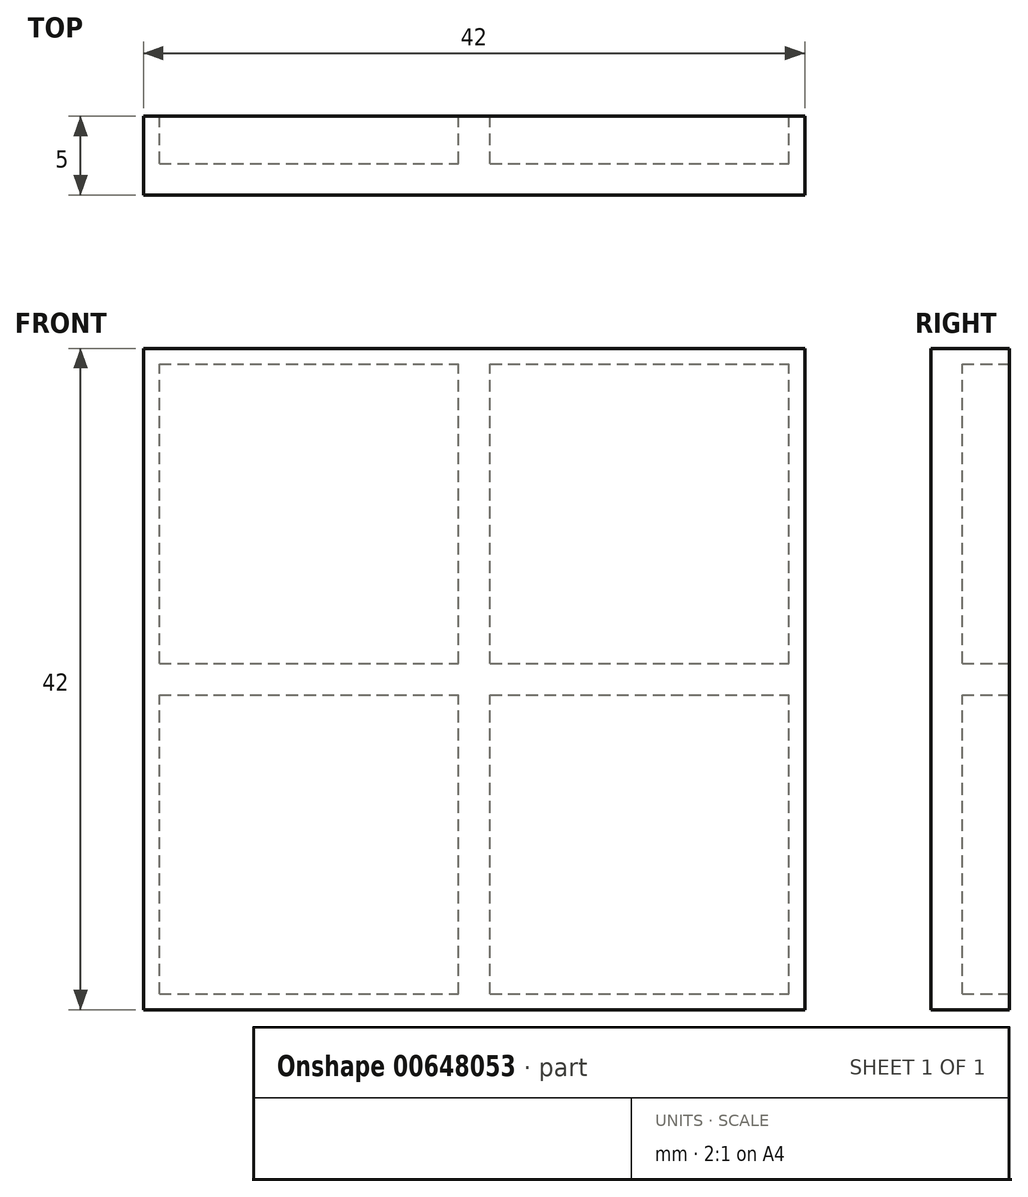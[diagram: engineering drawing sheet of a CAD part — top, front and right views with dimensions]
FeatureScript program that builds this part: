
annotation { "Feature Type Name" : "Feature", "Feature Type Description" : "" }
export const myFeature = defineFeature(function(context is Context, id is Id, definition is map)
    precondition{}
    {
        {
            var Q0;
            Q0=qCreatedBy(makeId("Front.planeOp"),FACE);
            var sketch = newSketch(context, id + "F0", { "sketchPlane" : qUnion([Q0])});
            skLineSegment(sketch, "E0.bottom", {"start": v(-21, 21) * mm, "end": v(21, 21) * mm});
            skLineSegment(sketch, "E0.top", {"start": v(-21, -21) * mm, "end": v(21, -21) * mm});
            skLineSegment(sketch, "E0.left", {"start": v(-21, 21) * mm, "end": v(-21, -21) * mm});
            skLineSegment(sketch, "E0.right", {"start": v(21, 21) * mm, "end": v(21, -21) * mm});
            skPoint(sketch, "E0.middle", {"position": v(0, 0) * mm});
            skSolve(sketch);
        }
        {
            var Q0;
            Q0=makeQuery(id+"F0.imprint","IMPRINT",FACE,{"disambiguationData":[TD([[makeQuery(id+"F0.imprint","IMPRINT",EDGE,{"derivedFrom":sQuery(id+"F0.wireOp",EDGE,"E0.bottom")}),-1.0]])]});
            extrude(context, id + "F1", {"entities" : qUnion([Q0]), "depth" : 5 * mm, "offsetDistance" : 25 * mm});
        }
        {
            var Q0;
            Q0=makeQuery(id+"F1.opExtrude","CAP_FACE",FACE,{"disambiguationData":[OSD([sQuery(id+"F0.wireOp",EDGE,"E0.bottom"),sQuery(id+"F0.wireOp",EDGE,"E0.top"),sQuery(id+"F0.wireOp",EDGE,"E0.left"),sQuery(id+"F0.wireOp",EDGE,"E0.right")])],"isStart":true});
            var sketch = newSketch(context, id + "F2", { "sketchPlane" : qUnion([Q0])});
            skLineSegment(sketch, "E1", {"start": v(-21, 21) * mm, "end": v(0, 0) * mm});
            skLineSegment(sketch, "E2", {"start": v(0, 21) * mm, "end": v(-21, 0) * mm});
            skPoint(sketch, "E3", {"position": v(-10.5, 10.5) * mm});
            skLineSegment(sketch, "E4", {"start": v(0, 21) * mm, "end": v(21, 0) * mm});
            skLineSegment(sketch, "E5", {"start": v(21, 21) * mm, "end": v(0, 0) * mm});
            skPoint(sketch, "E6", {"position": v(10.5, 10.5) * mm});
            skLineSegment(sketch, "E7", {"start": v(-21, 0) * mm, "end": v(0, -21) * mm});
            skLineSegment(sketch, "E8", {"start": v(0, 0) * mm, "end": v(-21, -21) * mm});
            skPoint(sketch, "E9", {"position": v(-10.5, -10.5) * mm});
            skLineSegment(sketch, "E10", {"start": v(0, 0) * mm, "end": v(21, -21) * mm});
            skLineSegment(sketch, "E11", {"start": v(21, 0) * mm, "end": v(0, -21) * mm});
            skPoint(sketch, "E12", {"position": v(10.5, -10.5) * mm});
            skLineSegment(sketch, "E13.bottom", {"start": v(20, 1) * mm, "end": v(1, 1) * mm});
            skLineSegment(sketch, "E13.top", {"start": v(20, 20) * mm, "end": v(1, 20) * mm});
            skLineSegment(sketch, "E13.left", {"start": v(20, 1) * mm, "end": v(20, 20) * mm});
            skLineSegment(sketch, "E13.right", {"start": v(1, 1) * mm, "end": v(1, 20) * mm});
            skLineSegment(sketch, "E14.bottom", {"start": v(-1, 1) * mm, "end": v(-20, 1) * mm});
            skLineSegment(sketch, "E14.top", {"start": v(-1, 20) * mm, "end": v(-20, 20) * mm});
            skLineSegment(sketch, "E14.left", {"start": v(-1, 1) * mm, "end": v(-1, 20) * mm});
            skLineSegment(sketch, "E14.right", {"start": v(-20, 1) * mm, "end": v(-20, 20) * mm});
            skLineSegment(sketch, "E15.bottom", {"start": v(20, -20) * mm, "end": v(1, -20) * mm});
            skLineSegment(sketch, "E15.top", {"start": v(20, -1) * mm, "end": v(1, -1) * mm});
            skLineSegment(sketch, "E15.left", {"start": v(20, -20) * mm, "end": v(20, -1) * mm});
            skLineSegment(sketch, "E15.right", {"start": v(1, -20) * mm, "end": v(1, -1) * mm});
            skPoint(sketch, "E16.middle", {"position": v(-1.23, -7.27) * mm});
            skLineSegment(sketch, "E17.bottom", {"start": v(-1, -20) * mm, "end": v(-20, -20) * mm});
            skLineSegment(sketch, "E17.top", {"start": v(-1, -1) * mm, "end": v(-20, -1) * mm});
            skLineSegment(sketch, "E17.left", {"start": v(-1, -20) * mm, "end": v(-1, -1) * mm});
            skLineSegment(sketch, "E17.right", {"start": v(-20, -20) * mm, "end": v(-20, -1) * mm});
            skSolve(sketch);
        }
        {
            var Q0;
            {var subQ0=sQuery(id+"F2.wireOp",EDGE,"E14.right");Q0=makeQuery(id+"F2.imprint","IMPRINT",FACE,{"disambiguationData":[TD([[makeQuery(id+"F2.imprint","IMPRINT",EDGE,{"derivedFrom":subQ0}),-1.0]])]});}
            var Q1;
            {var subQ0=sQuery(id+"F2.wireOp",EDGE,"E14.bottom");Q1=makeQuery(id+"F2.imprint","IMPRINT",FACE,{"disambiguationData":[TD([[makeQuery(id+"F2.imprint","IMPRINT",EDGE,{"derivedFrom":subQ0}),-1.0]])]});}
            var Q2;
            {var subQ0=sQuery(id+"F2.wireOp",EDGE,"E14.left");Q2=makeQuery(id+"F2.imprint","IMPRINT",FACE,{"disambiguationData":[TD([[makeQuery(id+"F2.imprint","IMPRINT",EDGE,{"derivedFrom":subQ0}),1.0]])]});}
            var Q3;
            {var subQ0=sQuery(id+"F2.wireOp",EDGE,"E14.top");Q3=makeQuery(id+"F2.imprint","IMPRINT",FACE,{"disambiguationData":[TD([[makeQuery(id+"F2.imprint","IMPRINT",EDGE,{"derivedFrom":subQ0}),1.0]])]});}
            var Q4;
            {var subQ0=sQuery(id+"F2.wireOp",EDGE,"E13.bottom");Q4=makeQuery(id+"F2.imprint","IMPRINT",FACE,{"disambiguationData":[TD([[makeQuery(id+"F2.imprint","IMPRINT",EDGE,{"derivedFrom":subQ0}),-1.0]])]});}
            var Q5;
            {var subQ0=sQuery(id+"F2.wireOp",EDGE,"E13.left");Q5=makeQuery(id+"F2.imprint","IMPRINT",FACE,{"disambiguationData":[TD([[makeQuery(id+"F2.imprint","IMPRINT",EDGE,{"derivedFrom":subQ0}),1.0]])]});}
            var Q6;
            {var subQ0=sQuery(id+"F2.wireOp",EDGE,"E13.right");Q6=makeQuery(id+"F2.imprint","IMPRINT",FACE,{"disambiguationData":[TD([[makeQuery(id+"F2.imprint","IMPRINT",EDGE,{"derivedFrom":subQ0}),-1.0]])]});}
            var Q7;
            {var subQ0=sQuery(id+"F2.wireOp",EDGE,"E13.top");Q7=makeQuery(id+"F2.imprint","IMPRINT",FACE,{"disambiguationData":[TD([[makeQuery(id+"F2.imprint","IMPRINT",EDGE,{"derivedFrom":subQ0}),1.0]])]});}
            var Q8;
            {var subQ0=sQuery(id+"F2.wireOp",EDGE,"E15.top");Q8=makeQuery(id+"F2.imprint","IMPRINT",FACE,{"disambiguationData":[TD([[makeQuery(id+"F2.imprint","IMPRINT",EDGE,{"derivedFrom":subQ0}),1.0]])]});}
            var Q9;
            {var subQ0=sQuery(id+"F2.wireOp",EDGE,"E15.right");Q9=makeQuery(id+"F2.imprint","IMPRINT",FACE,{"disambiguationData":[TD([[makeQuery(id+"F2.imprint","IMPRINT",EDGE,{"derivedFrom":subQ0}),-1.0]])]});}
            var Q10;
            {var subQ0=sQuery(id+"F2.wireOp",EDGE,"E15.left");Q10=makeQuery(id+"F2.imprint","IMPRINT",FACE,{"disambiguationData":[TD([[makeQuery(id+"F2.imprint","IMPRINT",EDGE,{"derivedFrom":subQ0}),1.0]])]});}
            var Q11;
            {var subQ0=sQuery(id+"F2.wireOp",EDGE,"E17.bottom");Q11=makeQuery(id+"F2.imprint","IMPRINT",FACE,{"disambiguationData":[TD([[makeQuery(id+"F2.imprint","IMPRINT",EDGE,{"derivedFrom":subQ0}),-1.0]])]});}
            var Q12;
            {var subQ0=sQuery(id+"F2.wireOp",EDGE,"E15.bottom");Q12=makeQuery(id+"F2.imprint","IMPRINT",FACE,{"disambiguationData":[TD([[makeQuery(id+"F2.imprint","IMPRINT",EDGE,{"derivedFrom":subQ0}),-1.0]])]});}
            var Q13;
            {var subQ0=sQuery(id+"F2.wireOp",EDGE,"E17.left");Q13=makeQuery(id+"F2.imprint","IMPRINT",FACE,{"disambiguationData":[TD([[makeQuery(id+"F2.imprint","IMPRINT",EDGE,{"derivedFrom":subQ0}),1.0]])]});}
            var Q14;
            {var subQ0=sQuery(id+"F2.wireOp",EDGE,"E17.top");Q14=makeQuery(id+"F2.imprint","IMPRINT",FACE,{"disambiguationData":[TD([[makeQuery(id+"F2.imprint","IMPRINT",EDGE,{"derivedFrom":subQ0}),1.0]])]});}
            var Q15;
            {var subQ0=sQuery(id+"F2.wireOp",EDGE,"E17.right");Q15=makeQuery(id+"F2.imprint","IMPRINT",FACE,{"disambiguationData":[TD([[makeQuery(id+"F2.imprint","IMPRINT",EDGE,{"derivedFrom":subQ0}),-1.0]])]});}
            extrude(context, id + "F3", {"entities" : qUnion([Q0, Q1, Q2, Q3, Q4, Q5, Q6, Q7, Q8, Q9, Q10, Q11, Q12, Q13, Q14, Q15]), "operationType" : NewBodyOperationType.REMOVE, "oppositeDirection" : true, "depth" : 3 * mm, "offsetDistance" : 25 * mm});
        }
    });
